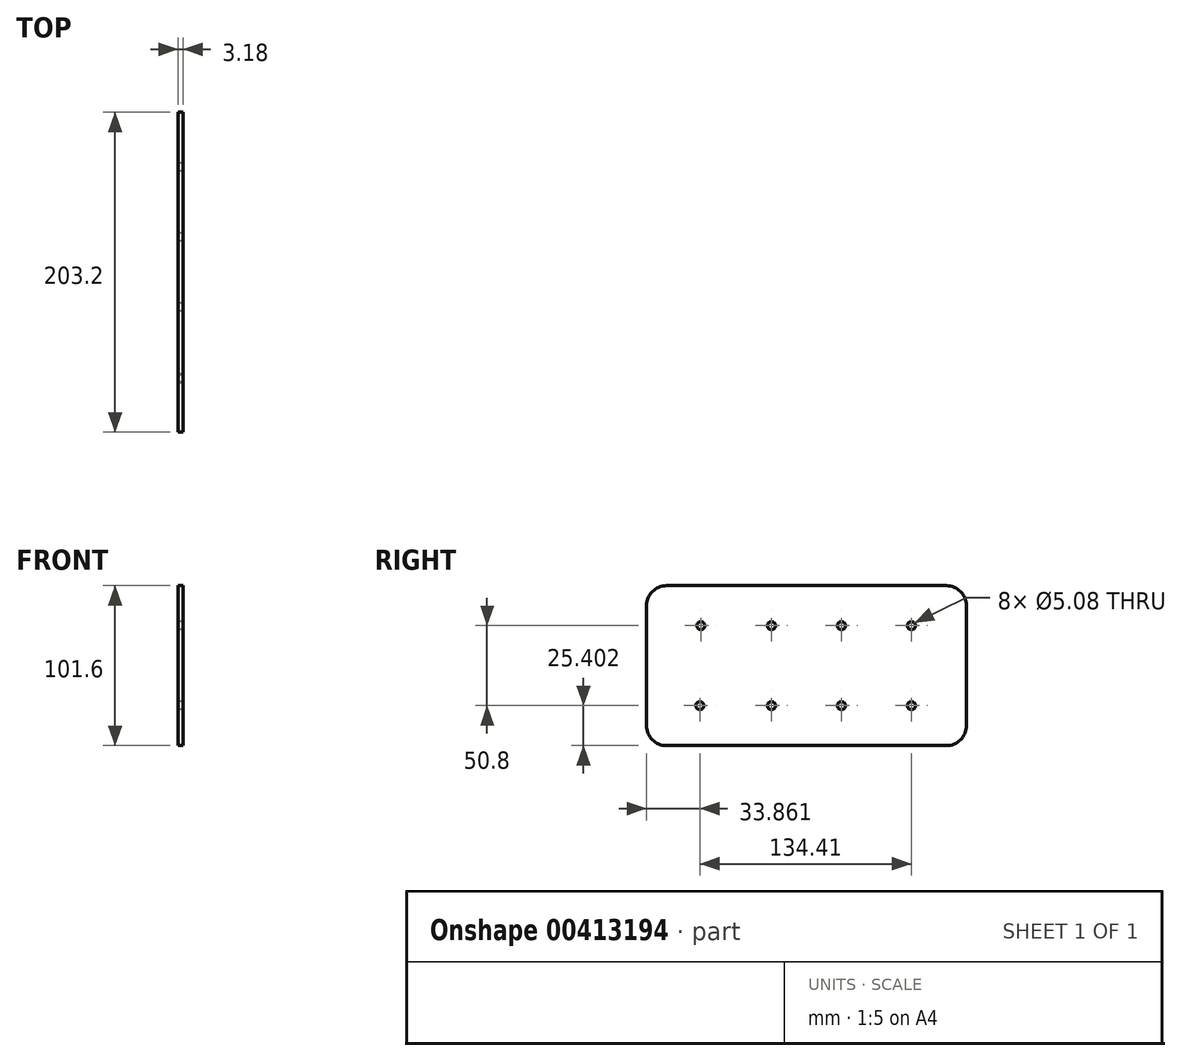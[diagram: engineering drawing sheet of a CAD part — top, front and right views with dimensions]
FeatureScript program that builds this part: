
annotation { "Feature Type Name" : "Feature", "Feature Type Description" : "" }
export const myFeature = defineFeature(function(context is Context, id is Id, definition is map)
    precondition{}
    {
        {
            var Q0;
            Q0=qCreatedBy(makeId("Right.planeOp"),FACE);
            var sketch = newSketch(context, id + "F0", { "sketchPlane" : qUnion([Q0])});
            skLineSegment(sketch, "E0.bottom", {"start": v(78.57, -276.8) * mm, "end": v(256.37, -276.8) * mm});
            skLineSegment(sketch, "E0.top", {"start": v(78.57, -378.4) * mm, "end": v(256.37, -378.4) * mm});
            skLineSegment(sketch, "E0.left", {"start": v(65.87, -289.5) * mm, "end": v(65.87, -365.7) * mm});
            skLineSegment(sketch, "E0.right", {"start": v(269.07, -289.5) * mm, "end": v(269.07, -365.7) * mm});
            skPoint(sketch, "E1.visualSharp", {"position": v(65.87, -276.8) * mm});
            skArc(sketch, "E1.filletArc", {"start": v(78.57, -276.8) * mm, "mid": v(69.59, -280.53) * mm, "end": v(65.87, -289.5) * mm});
            skPoint(sketch, "E2.visualSharp", {"position": v(65.87, -378.4) * mm});
            skArc(sketch, "E2.filletArc", {"start": v(65.87, -365.7) * mm, "mid": v(69.59, -374.69) * mm, "end": v(78.57, -378.4) * mm});
            skPoint(sketch, "E3.visualSharp", {"position": v(269.07, -378.4) * mm});
            skArc(sketch, "E3.filletArc", {"start": v(256.37, -378.4) * mm, "mid": v(265.35, -374.69) * mm, "end": v(269.07, -365.7) * mm});
            skPoint(sketch, "E4.visualSharp", {"position": v(269.07, -276.8) * mm});
            skArc(sketch, "E4.filletArc", {"start": v(269.07, -289.5) * mm, "mid": v(265.35, -280.53) * mm, "end": v(256.37, -276.8) * mm});
            skCircle(sketch, "E5", {"center": v(100.38, -302.2) * mm, "radius": 2.54 * mm});
            skCircle(sketch, "E6", {"center": v(145.24, -302.2) * mm, "radius": 2.54 * mm});
            skCircle(sketch, "E7", {"center": v(189.7, -302.2) * mm, "radius": 2.54 * mm});
            skCircle(sketch, "E8", {"center": v(234.14, -302.2) * mm, "radius": 2.54 * mm});
            skCircle(sketch, "E9", {"center": v(99.73, -353) * mm, "radius": 2.54 * mm});
            skCircle(sketch, "E10", {"center": v(145.24, -353) * mm, "radius": 2.54 * mm});
            skCircle(sketch, "E11", {"center": v(189.7, -353) * mm, "radius": 2.54 * mm});
            skCircle(sketch, "E12", {"center": v(234.14, -353) * mm, "radius": 2.54 * mm});
            skSolve(sketch);
        }
        {
            var Q0;
            Q0=makeQuery(id+"F0.imprint","IMPRINT",FACE,{"disambiguationData":[TD([[makeQuery(id+"F0.imprint","IMPRINT",EDGE,{"derivedFrom":sQuery(id+"F0.wireOp",EDGE,"E0.bottom")}),-1.0]])]});
            extrude(context, id + "F1", {"entities" : qUnion([Q0]), "depth" : 3.17 * mm});
        }
    });
